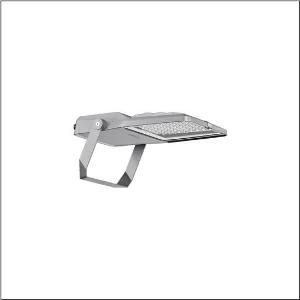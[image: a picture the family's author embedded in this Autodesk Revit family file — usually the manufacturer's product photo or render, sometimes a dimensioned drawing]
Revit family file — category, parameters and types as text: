
# Revit family: floodlight_fl_21_iq_mini___pl43_5xa7772d1a1a_00f7
name_source: partatom
category: Lighting Fixtures
units: mm (PartAtom-declared; Revit-internal decimal feet)

## family parameters
Cut with Voids When Loaded = No
Host = Face
Light Source = No
Part Type = Normal
Room Calculation Point = No
Round Connector Dimension = Use Diameter
Shared = No

## types (1)
- --- (1 x LED, 15140 lm, 143 W, 2200K)
    Apparent Load = 143 VA
    CIE Flux Codes = 27 78 99 100 100
    Color Rendering = 70
    Color Temperature = 2200K
    Default Elevation = 1800 mm
    Description = Floodlight FL 21 iQ mini, floodlight, primary light control with lens, of PMMA, primary optical cover: protective disc, of toughened safety glass, transparent, light distribution: PL43, light emission: direct distribution, installation type: surface-mounted, lamps: LED, High Power LED, rated values: 15.140lm | 143W | 105,9lm/W (begin service life); end service life: 15.140lm | 151,6W; at 50% lumin. flux: 7.570lm | 60,5W | 125,1lm/W, colour temperature: 2200K, colour rendering: CRI > 70, light colour: 722, light setting 1 begin service life: 100% | 15.140lm | 143W | 105,9lm/W | 2.200K, light setting 1 end service life: 151,6W, further light settings possible, control: Street-Remote, Auto-Match, Temp-Guard, Night-Set, Smart-Wire, Desk-Remote (wireless, voltage-free reading and setting of iQ features in the workshop via application-optimized NFC function/RFID function), optimised constant luminous flux control (CLO 2.0), pre-setting: linear dimming characteristic, with terminal, 6-pole, mains connection: 220..240V, AC, 50/60Hz, luminaire housing, of diecast aluminium, powder-coated, SITECO metallic grey (DB 702S), corrosivity category C5 mid according to DIN EN ISO 12944suitable for swimming poolschlorine-resistant, sealing non-destructively replaceable, mounting bracket, of steel, galvanised, powder-coated, SITECO metallic grey (DB 702S), protection rating (complete): IP66, insulation class (complete): insulation class II (safety insulation), certification: CE, ENEC, VDE, protection symbol: D, impact resistance: IK08, permissible operating ambient temperature: -40..+40°C, permissible operating ambient temperature for outdoor applications: -40..+50°C, standard: DIN EN 12944, LABS conformity tested according to VDMA 24364:2018-05, packaging unit: 1 piece

Light Distribution: PL43
    Height = 70 mm
    Lamp = 1 x LED
    Lamp Light Flux = 15140 lm
    Lamp Power = 143 W
    Lamp count = 1
    Length = 485 mm
    Luminous efficacy = 106 lm/W
    Manufacturer = Siteco
    ModVariant = No
    Model = 5XA7772D1A1A
    Mounting Place = Pole
    Mounting Type = Pole annexe
    Number of Poles = 1
    OnlyDefault = Yes
    Power Factor = 1
    Product Name = Floodlight FL 21 iQ mini | PL43
    Product group = floodlight | pylon annexe
    ProductGroupID = 6201
    Protection Class = Protection class II
    Protection Degree = IP 66
    RLX_Detail_Level = 1
    RLX_Emergency_Light_Flux = 0 lm
    RLX_Emergency_Type = 0
    RLX_Emergency_Type_DB = No
    RlxData = <blob elided: 96609 chars, md5=07b1bfee>
    Socket = socket
    Standby Power = 0 W
    System Light Flux = 15140 lm
    System Power = 143 W
    Type Comments = factory setting: luminous flux: 100 % | dim-lin: 254 | 730 mA
    Type Image = l_1006845.jpg
    URL = http://relux.com
    VarID = @adj_162733
    Voltage = 0 V
    Weight = 0.00 kg
    Width = 337 mm

## geometry (parser evidence)
native form markers: Blend x4, Sweep x12
no freeform markers — native parametric forms only
